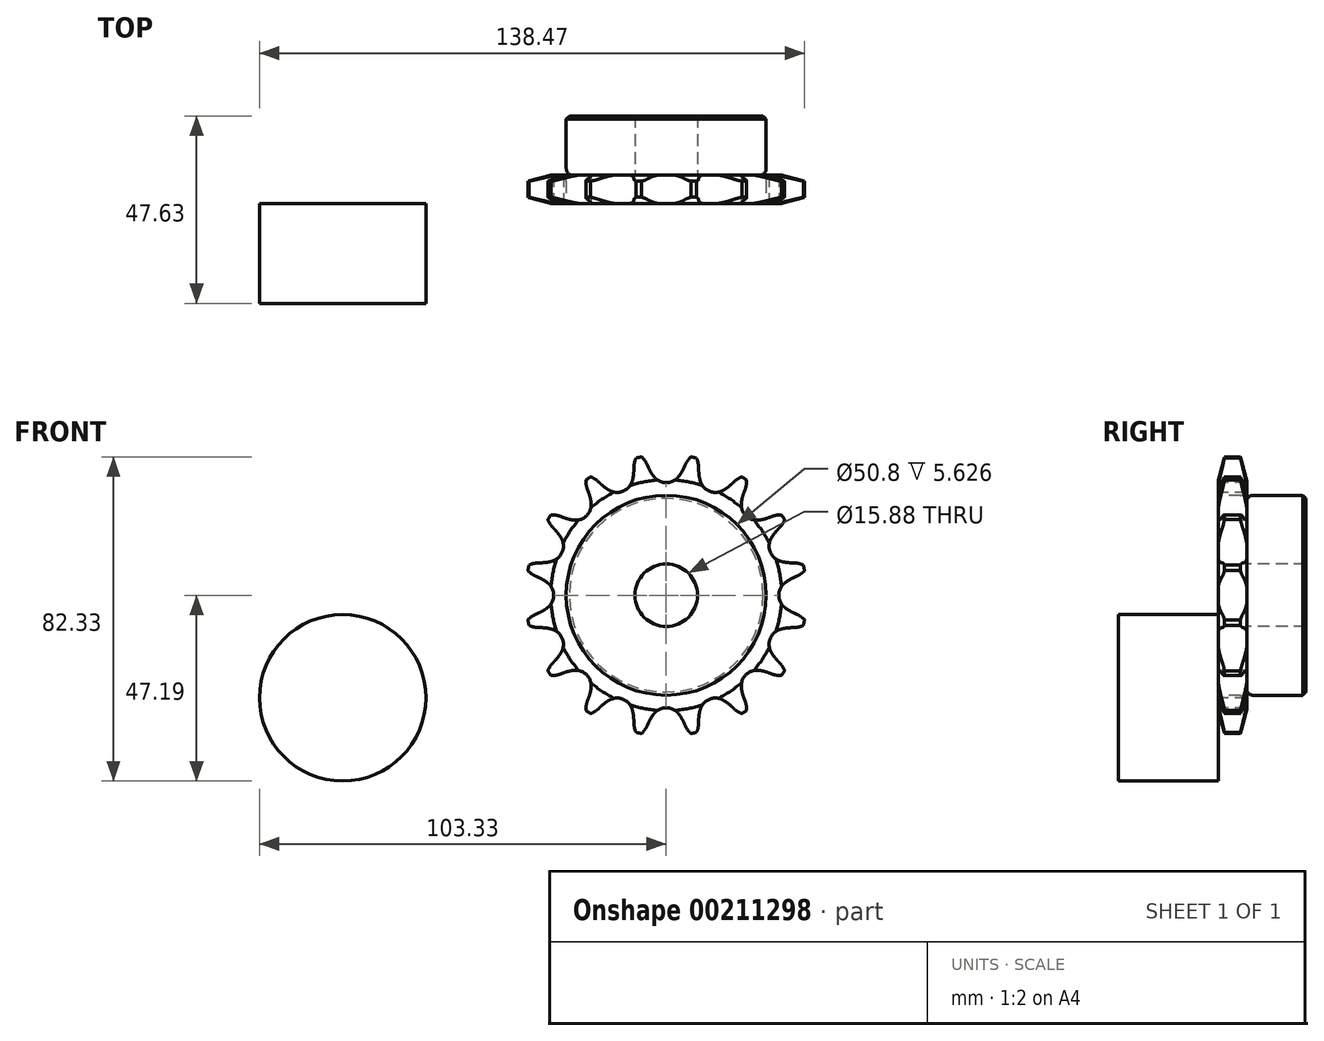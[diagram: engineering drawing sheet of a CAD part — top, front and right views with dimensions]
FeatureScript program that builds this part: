
annotation { "Feature Type Name" : "Feature", "Feature Type Description" : "" }
export const myFeature = defineFeature(function(context is Context, id is Id, definition is map)
    precondition{}
    {
        {
            var Q0;
            Q0=qCreatedBy(makeId("Right.planeOp"),FACE);
            var sketch = newSketch(context, id + "F0", { "sketchPlane" : qUnion([Q0])});
            skLineSegment(sketch, "E0", {"start": v(0, 0) * mm, "end": v(22.23, 0) * mm, "construction": true});
            skLineSegment(sketch, "E1.bottom", {"start": v(0, 7.94) * mm, "end": v(7.21, 7.94) * mm});
            skLineSegment(sketch, "E1.top", {"start": v(0, 35.69) * mm, "end": v(7.21, 35.69) * mm});
            skLineSegment(sketch, "E1.left", {"start": v(0, 7.94) * mm, "end": v(0, 35.69) * mm});
            skLineSegment(sketch, "E1.right", {"start": v(7.21, 7.94) * mm, "end": v(7.21, 35.69) * mm});
            skLineSegment(sketch, "E2.bottom", {"start": v(0, 7.94) * mm, "end": v(22.23, 7.94) * mm});
            skLineSegment(sketch, "E2.top", {"start": v(0, 25.4) * mm, "end": v(22.23, 25.4) * mm});
            skLineSegment(sketch, "E2.left", {"start": v(0, 7.94) * mm, "end": v(0, 25.4) * mm});
            skLineSegment(sketch, "E2.right", {"start": v(22.23, 7.94) * mm, "end": v(22.23, 25.4) * mm});
            skLineSegment(sketch, "E3.MirrorCS", {"start": v(0, -7.94) * mm, "end": v(7.21, -7.94) * mm});
            skLineSegment(sketch, "E4.MirrorCS", {"start": v(0, -25.4) * mm, "end": v(22.23, -25.4) * mm});
            skLineSegment(sketch, "E5.MirrorCS", {"start": v(0, -7.94) * mm, "end": v(22.23, -7.94) * mm});
            skLineSegment(sketch, "E6.MirrorCS", {"start": v(7.21, -7.94) * mm, "end": v(7.21, -35.69) * mm});
            skLineSegment(sketch, "E7.MirrorCS", {"start": v(0, -7.94) * mm, "end": v(0, -35.69) * mm});
            skLineSegment(sketch, "E8.MirrorCS", {"start": v(22.23, -7.94) * mm, "end": v(22.23, -25.4) * mm});
            skLineSegment(sketch, "E9.MirrorCS", {"start": v(0, -7.94) * mm, "end": v(0, -25.4) * mm});
            skLineSegment(sketch, "E10.MirrorCS", {"start": v(0, -35.69) * mm, "end": v(7.21, -35.69) * mm});
            skSolve(sketch);
        }
        {
            var Q0;
            {var subQ0=sQuery(id+"F0.wireOp",EDGE,"E1.top");Q0=makeQuery(id+"F0.imprint","IMPRINT",FACE,{"disambiguationData":[TD([[makeQuery(id+"F0.imprint","IMPRINT",EDGE,{"derivedFrom":subQ0}),-1.0]])]});}
            var Q1;
            {var subQ5=sQuery(id+"F0.wireOp",EDGE,"E2.left");Q1=makeQuery(id+"F0.imprint","IMPRINT",FACE,{"disambiguationData":[TD([[makeQuery(id+"F0.imprint","IMPRINT",EDGE,{"derivedFrom":subQ5}),-1.0]])]});}
            var Q2;
            {var subQ5=sQuery(id+"F0.wireOp",EDGE,"E2.right");Q2=makeQuery(id+"F0.imprint","IMPRINT",FACE,{"disambiguationData":[TD([[makeQuery(id+"F0.imprint","IMPRINT",EDGE,{"derivedFrom":subQ5}),1.0]])]});}
            var Q3;
            Q3=sQuery(id+"F0.wireOp",EDGE,"E0");
            revolve(context, id + "F1", {"entities" : qUnion([Q0, Q1, Q2]), "axis" : qUnion([Q3]), "revolveType" : RevolveType.FULL});
        }
        {
            var Q0;
            Q0=makeQuery(id+"F1.opRevolve","SWEPT_EDGE",EDGE,{"disambiguationData":[OSD([sQuery(id+"F0.wireOp",EDGE,"E1.right"),sQuery(id+"F0.wireOp",EDGE,"E2.top")])]});
            fillet(context, id + "F2", {"entities" : qUnion([Q0]), "radius" : 1.59 * mm, "tangentPropagation" : true, "allowEdgeOverflow" : false});
        }
        {
            var Q0;
            Q0=makeQuery(id+"F1.opRevolve","SWEPT_EDGE",EDGE,{"disambiguationData":[OSD([sQuery(id+"F0.wireOp",EDGE,"E2.top"),sQuery(id+"F0.wireOp",EDGE,"E2.right")])]});
            chamfer(context, id + "F3", {"entities" : qUnion([Q0]), "width" : 0.8 * mm, "tangentPropagation" : true});
        }
        {
            var Q0;
            Q0=makeQuery(id+"F1.opRevolve","SWEPT_EDGE",EDGE,{"disambiguationData":[OSD([sQuery(id+"F0.wireOp",EDGE,"E1.top"),sQuery(id+"F0.wireOp",EDGE,"E1.left")])]});
            var Q1;
            Q1=makeQuery(id+"F1.opRevolve","SWEPT_EDGE",EDGE,{"disambiguationData":[OSD([sQuery(id+"F0.wireOp",EDGE,"E1.top"),sQuery(id+"F0.wireOp",EDGE,"E1.right")])]});
            chamfer(context, id + "F4", {"entities" : qUnion([Q0, Q1]), "chamferType" : ChamferType.TWO_OFFSETS, "width1" : 6.35 * mm, "oppositeDirection" : false, "width2" : 1.57 * mm, "tangentPropagation" : true});
        }
        {
            var Q0;
            Q0=makeQuery(id+"F1.opRevolve","SWEPT_FACE",FACE,{"disambiguationData":[OSD([sQuery(id+"F0.wireOp",EDGE,"E1.left"),sQuery(id+"F0.wireOp",EDGE,"E2.left")])]});
            var sketch = newSketch(context, id + "F5", { "sketchPlane" : qUnion([Q0])});
            skArc(sketch, "E11", {"start": v(-4.8, 33.1) * mm, "mid": v(-5.78, 34.65) * mm, "end": v(-7.13, 35.87) * mm});
            skLineSegment(sketch, "E12", {"start": v(-4.45, 32.3) * mm, "end": v(-4.8, 33.1) * mm});
            skArc(sketch, "E13", {"start": v(-4.45, 32.3) * mm, "mid": v(-3.84, 31.15) * mm, "end": v(-3.1, 30.08) * mm});
            skArc(sketch, "E14", {"start": v(-3.1, 30.08) * mm, "mid": v(0.01, 28.6) * mm, "end": v(3.1, 30.1) * mm});
            skArc(sketch, "E15.MirrorCS", {"start": v(4.46, 32.32) * mm, "mid": v(3.85, 31.17) * mm, "end": v(3.1, 30.1) * mm});
            skLineSegment(sketch, "E16.MirrorCS", {"start": v(4.46, 32.32) * mm, "end": v(4.82, 33.12) * mm});
            skArc(sketch, "E17.MirrorCS", {"start": v(4.82, 33.12) * mm, "mid": v(5.79, 34.66) * mm, "end": v(7.14, 35.87) * mm});
            skLineSegment(sketch, "E18", {"start": v(0, 0) * mm, "end": v(0, 32.56) * mm, "construction": true});
            skArc(sketch, "E19.1.0", {"start": v(-17.1, 28.74) * mm, "mid": v(-18.6, 29.8) * mm, "end": v(-20.32, 30.41) * mm});
            skLineSegment(sketch, "E19.1.1", {"start": v(-16.47, 28.14) * mm, "end": v(-17.1, 28.74) * mm});
            skArc(sketch, "E19.1.2", {"start": v(-16.47, 28.14) * mm, "mid": v(-15.47, 27.3) * mm, "end": v(-14.37, 26.61) * mm});
            skArc(sketch, "E19.1.3", {"start": v(-14.37, 26.61) * mm, "mid": v(-10.93, 26.43) * mm, "end": v(-8.65, 29) * mm});
            skArc(sketch, "E19.1.4", {"start": v(-8.25, 31.57) * mm, "mid": v(-8.37, 30.27) * mm, "end": v(-8.65, 29) * mm});
            skLineSegment(sketch, "E19.1.5", {"start": v(-8.25, 31.57) * mm, "end": v(-8.22, 32.44) * mm});
            skArc(sketch, "E19.1.6", {"start": v(-8.22, 32.44) * mm, "mid": v(-7.91, 34.23) * mm, "end": v(-7.13, 35.87) * mm});
            skArc(sketch, "E19.2.0", {"start": v(-26.8, 20) * mm, "mid": v(-28.59, 20.42) * mm, "end": v(-30.4, 20.32) * mm});
            skLineSegment(sketch, "E19.2.1", {"start": v(-25.99, 19.7) * mm, "end": v(-26.8, 20) * mm});
            skArc(sketch, "E19.2.2", {"start": v(-25.99, 19.7) * mm, "mid": v(-24.74, 19.31) * mm, "end": v(-23.46, 19.09) * mm});
            skArc(sketch, "E19.2.3", {"start": v(-23.46, 19.09) * mm, "mid": v(-20.22, 20.23) * mm, "end": v(-19.09, 23.48) * mm});
            skArc(sketch, "E19.2.4", {"start": v(-19.7, 26.01) * mm, "mid": v(-19.31, 24.76) * mm, "end": v(-19.09, 23.48) * mm});
            skLineSegment(sketch, "E19.2.5", {"start": v(-19.7, 26.01) * mm, "end": v(-20, 26.83) * mm});
            skArc(sketch, "E19.2.6", {"start": v(-20, 26.83) * mm, "mid": v(-20.41, 28.6) * mm, "end": v(-20.32, 30.41) * mm});
            skArc(sketch, "E19.3.0", {"start": v(-32.42, 8.22) * mm, "mid": v(-34.22, 7.92) * mm, "end": v(-35.87, 7.14) * mm});
            skLineSegment(sketch, "E19.3.1", {"start": v(-31.55, 8.25) * mm, "end": v(-32.42, 8.22) * mm});
            skArc(sketch, "E19.3.2", {"start": v(-31.55, 8.25) * mm, "mid": v(-30.25, 8.37) * mm, "end": v(-28.98, 8.66) * mm});
            skArc(sketch, "E19.3.3", {"start": v(-28.98, 8.66) * mm, "mid": v(-26.42, 10.96) * mm, "end": v(-26.62, 14.39) * mm});
            skArc(sketch, "E19.3.4", {"start": v(-28.15, 16.5) * mm, "mid": v(-27.32, 15.49) * mm, "end": v(-26.62, 14.39) * mm});
            skLineSegment(sketch, "E19.3.5", {"start": v(-28.15, 16.5) * mm, "end": v(-28.75, 17.13) * mm});
            skArc(sketch, "E19.3.6", {"start": v(-28.75, 17.13) * mm, "mid": v(-29.8, 18.61) * mm, "end": v(-30.4, 20.32) * mm});
            skArc(sketch, "E19.4.0", {"start": v(-33.1, -4.8) * mm, "mid": v(-34.65, -5.78) * mm, "end": v(-35.87, -7.13) * mm});
            skLineSegment(sketch, "E19.4.1", {"start": v(-32.3, -4.45) * mm, "end": v(-33.1, -4.8) * mm});
            skArc(sketch, "E19.4.2", {"start": v(-32.3, -4.45) * mm, "mid": v(-31.15, -3.84) * mm, "end": v(-30.08, -3.1) * mm});
            skArc(sketch, "E19.4.3", {"start": v(-30.08, -3.1) * mm, "mid": v(-28.6, 0.01) * mm, "end": v(-30.1, 3.1) * mm});
            skArc(sketch, "E19.4.4", {"start": v(-32.32, 4.46) * mm, "mid": v(-31.17, 3.85) * mm, "end": v(-30.1, 3.1) * mm});
            skLineSegment(sketch, "E19.4.5", {"start": v(-32.32, 4.46) * mm, "end": v(-33.12, 4.82) * mm});
            skArc(sketch, "E19.4.6", {"start": v(-33.12, 4.82) * mm, "mid": v(-34.66, 5.79) * mm, "end": v(-35.87, 7.14) * mm});
            skArc(sketch, "E19.5.0", {"start": v(-28.74, -17.1) * mm, "mid": v(-29.8, -18.6) * mm, "end": v(-30.41, -20.32) * mm});
            skLineSegment(sketch, "E19.5.1", {"start": v(-28.14, -16.47) * mm, "end": v(-28.74, -17.1) * mm});
            skArc(sketch, "E19.5.2", {"start": v(-28.14, -16.47) * mm, "mid": v(-27.3, -15.47) * mm, "end": v(-26.61, -14.37) * mm});
            skArc(sketch, "E19.5.3", {"start": v(-26.61, -14.37) * mm, "mid": v(-26.43, -10.93) * mm, "end": v(-29, -8.65) * mm});
            skArc(sketch, "E19.5.4", {"start": v(-31.57, -8.25) * mm, "mid": v(-30.27, -8.37) * mm, "end": v(-29, -8.65) * mm});
            skLineSegment(sketch, "E19.5.5", {"start": v(-31.57, -8.25) * mm, "end": v(-32.44, -8.22) * mm});
            skArc(sketch, "E19.5.6", {"start": v(-32.44, -8.22) * mm, "mid": v(-34.23, -7.91) * mm, "end": v(-35.87, -7.13) * mm});
            skArc(sketch, "E19.6.0", {"start": v(-20, -26.8) * mm, "mid": v(-20.42, -28.59) * mm, "end": v(-20.32, -30.4) * mm});
            skLineSegment(sketch, "E19.6.1", {"start": v(-19.7, -25.99) * mm, "end": v(-20, -26.8) * mm});
            skArc(sketch, "E19.6.2", {"start": v(-19.7, -25.99) * mm, "mid": v(-19.31, -24.74) * mm, "end": v(-19.09, -23.46) * mm});
            skArc(sketch, "E19.6.3", {"start": v(-19.09, -23.46) * mm, "mid": v(-20.23, -20.22) * mm, "end": v(-23.48, -19.09) * mm});
            skArc(sketch, "E19.6.4", {"start": v(-26.01, -19.7) * mm, "mid": v(-24.76, -19.31) * mm, "end": v(-23.48, -19.09) * mm});
            skLineSegment(sketch, "E19.6.5", {"start": v(-26.01, -19.7) * mm, "end": v(-26.83, -20) * mm});
            skArc(sketch, "E19.6.6", {"start": v(-26.83, -20) * mm, "mid": v(-28.6, -20.41) * mm, "end": v(-30.41, -20.32) * mm});
            skArc(sketch, "E19.7.0", {"start": v(-8.22, -32.42) * mm, "mid": v(-7.92, -34.22) * mm, "end": v(-7.14, -35.87) * mm});
            skLineSegment(sketch, "E19.7.1", {"start": v(-8.25, -31.55) * mm, "end": v(-8.22, -32.42) * mm});
            skArc(sketch, "E19.7.2", {"start": v(-8.25, -31.55) * mm, "mid": v(-8.37, -30.25) * mm, "end": v(-8.66, -28.98) * mm});
            skArc(sketch, "E19.7.3", {"start": v(-8.66, -28.98) * mm, "mid": v(-10.96, -26.42) * mm, "end": v(-14.39, -26.62) * mm});
            skArc(sketch, "E19.7.4", {"start": v(-16.5, -28.15) * mm, "mid": v(-15.49, -27.32) * mm, "end": v(-14.39, -26.62) * mm});
            skLineSegment(sketch, "E19.7.5", {"start": v(-16.5, -28.15) * mm, "end": v(-17.13, -28.75) * mm});
            skArc(sketch, "E19.7.6", {"start": v(-17.13, -28.75) * mm, "mid": v(-18.61, -29.8) * mm, "end": v(-20.32, -30.4) * mm});
            skArc(sketch, "E19.8.0", {"start": v(4.8, -33.1) * mm, "mid": v(5.78, -34.65) * mm, "end": v(7.13, -35.87) * mm});
            skLineSegment(sketch, "E19.8.1", {"start": v(4.45, -32.3) * mm, "end": v(4.8, -33.1) * mm});
            skArc(sketch, "E19.8.2", {"start": v(4.45, -32.3) * mm, "mid": v(3.84, -31.15) * mm, "end": v(3.1, -30.08) * mm});
            skArc(sketch, "E19.8.3", {"start": v(3.1, -30.08) * mm, "mid": v(-0.01, -28.6) * mm, "end": v(-3.1, -30.1) * mm});
            skArc(sketch, "E19.8.4", {"start": v(-4.46, -32.32) * mm, "mid": v(-3.85, -31.17) * mm, "end": v(-3.1, -30.1) * mm});
            skLineSegment(sketch, "E19.8.5", {"start": v(-4.46, -32.32) * mm, "end": v(-4.82, -33.12) * mm});
            skArc(sketch, "E19.8.6", {"start": v(-4.82, -33.12) * mm, "mid": v(-5.79, -34.66) * mm, "end": v(-7.14, -35.87) * mm});
            skArc(sketch, "E19.9.0", {"start": v(17.1, -28.74) * mm, "mid": v(18.6, -29.8) * mm, "end": v(20.32, -30.41) * mm});
            skLineSegment(sketch, "E19.9.1", {"start": v(16.47, -28.14) * mm, "end": v(17.1, -28.74) * mm});
            skArc(sketch, "E19.9.2", {"start": v(16.47, -28.14) * mm, "mid": v(15.47, -27.3) * mm, "end": v(14.37, -26.61) * mm});
            skArc(sketch, "E19.9.3", {"start": v(14.37, -26.61) * mm, "mid": v(10.93, -26.43) * mm, "end": v(8.65, -29) * mm});
            skArc(sketch, "E19.9.4", {"start": v(8.25, -31.57) * mm, "mid": v(8.37, -30.27) * mm, "end": v(8.65, -29) * mm});
            skLineSegment(sketch, "E19.9.5", {"start": v(8.25, -31.57) * mm, "end": v(8.22, -32.44) * mm});
            skArc(sketch, "E19.9.6", {"start": v(8.22, -32.44) * mm, "mid": v(7.91, -34.23) * mm, "end": v(7.13, -35.87) * mm});
            skArc(sketch, "E19.10.0", {"start": v(26.8, -20) * mm, "mid": v(28.59, -20.42) * mm, "end": v(30.4, -20.32) * mm});
            skLineSegment(sketch, "E19.10.1", {"start": v(25.99, -19.7) * mm, "end": v(26.8, -20) * mm});
            skArc(sketch, "E19.10.2", {"start": v(25.99, -19.7) * mm, "mid": v(24.74, -19.31) * mm, "end": v(23.46, -19.09) * mm});
            skArc(sketch, "E19.10.3", {"start": v(23.46, -19.09) * mm, "mid": v(20.22, -20.23) * mm, "end": v(19.09, -23.48) * mm});
            skArc(sketch, "E19.10.4", {"start": v(19.7, -26.01) * mm, "mid": v(19.31, -24.76) * mm, "end": v(19.09, -23.48) * mm});
            skLineSegment(sketch, "E19.10.5", {"start": v(19.7, -26.01) * mm, "end": v(20, -26.83) * mm});
            skArc(sketch, "E19.10.6", {"start": v(20, -26.83) * mm, "mid": v(20.41, -28.6) * mm, "end": v(20.32, -30.41) * mm});
            skArc(sketch, "E19.11.0", {"start": v(32.42, -8.22) * mm, "mid": v(34.22, -7.92) * mm, "end": v(35.87, -7.14) * mm});
            skLineSegment(sketch, "E19.11.1", {"start": v(31.55, -8.25) * mm, "end": v(32.42, -8.22) * mm});
            skArc(sketch, "E19.11.2", {"start": v(31.55, -8.25) * mm, "mid": v(30.25, -8.37) * mm, "end": v(28.98, -8.66) * mm});
            skArc(sketch, "E19.11.3", {"start": v(28.98, -8.66) * mm, "mid": v(26.42, -10.96) * mm, "end": v(26.62, -14.39) * mm});
            skArc(sketch, "E19.11.4", {"start": v(28.15, -16.5) * mm, "mid": v(27.32, -15.49) * mm, "end": v(26.62, -14.39) * mm});
            skLineSegment(sketch, "E19.11.5", {"start": v(28.15, -16.5) * mm, "end": v(28.75, -17.13) * mm});
            skArc(sketch, "E19.11.6", {"start": v(28.75, -17.13) * mm, "mid": v(29.8, -18.61) * mm, "end": v(30.4, -20.32) * mm});
            skArc(sketch, "E19.12.0", {"start": v(33.1, 4.8) * mm, "mid": v(34.65, 5.78) * mm, "end": v(35.87, 7.13) * mm});
            skLineSegment(sketch, "E19.12.1", {"start": v(32.3, 4.45) * mm, "end": v(33.1, 4.8) * mm});
            skArc(sketch, "E19.12.2", {"start": v(32.3, 4.45) * mm, "mid": v(31.15, 3.84) * mm, "end": v(30.08, 3.1) * mm});
            skArc(sketch, "E19.12.3", {"start": v(30.08, 3.1) * mm, "mid": v(28.6, -0.01) * mm, "end": v(30.1, -3.1) * mm});
            skArc(sketch, "E19.12.4", {"start": v(32.32, -4.46) * mm, "mid": v(31.17, -3.85) * mm, "end": v(30.1, -3.1) * mm});
            skLineSegment(sketch, "E19.12.5", {"start": v(32.32, -4.46) * mm, "end": v(33.12, -4.82) * mm});
            skArc(sketch, "E19.12.6", {"start": v(33.12, -4.82) * mm, "mid": v(34.66, -5.79) * mm, "end": v(35.87, -7.14) * mm});
            skArc(sketch, "E19.13.0", {"start": v(28.74, 17.1) * mm, "mid": v(29.8, 18.6) * mm, "end": v(30.41, 20.32) * mm});
            skLineSegment(sketch, "E19.13.1", {"start": v(28.14, 16.47) * mm, "end": v(28.74, 17.1) * mm});
            skArc(sketch, "E19.13.2", {"start": v(28.14, 16.47) * mm, "mid": v(27.3, 15.47) * mm, "end": v(26.61, 14.37) * mm});
            skArc(sketch, "E19.13.3", {"start": v(26.61, 14.37) * mm, "mid": v(26.43, 10.93) * mm, "end": v(29, 8.65) * mm});
            skArc(sketch, "E19.13.4", {"start": v(31.57, 8.25) * mm, "mid": v(30.27, 8.37) * mm, "end": v(29, 8.65) * mm});
            skLineSegment(sketch, "E19.13.5", {"start": v(31.57, 8.25) * mm, "end": v(32.44, 8.22) * mm});
            skArc(sketch, "E19.13.6", {"start": v(32.44, 8.22) * mm, "mid": v(34.23, 7.91) * mm, "end": v(35.87, 7.13) * mm});
            skArc(sketch, "E19.14.0", {"start": v(20, 26.8) * mm, "mid": v(20.42, 28.59) * mm, "end": v(20.32, 30.4) * mm});
            skLineSegment(sketch, "E19.14.1", {"start": v(19.7, 25.99) * mm, "end": v(20, 26.8) * mm});
            skArc(sketch, "E19.14.2", {"start": v(19.7, 25.99) * mm, "mid": v(19.31, 24.74) * mm, "end": v(19.09, 23.46) * mm});
            skArc(sketch, "E19.14.3", {"start": v(19.09, 23.46) * mm, "mid": v(20.23, 20.22) * mm, "end": v(23.48, 19.09) * mm});
            skArc(sketch, "E19.14.4", {"start": v(26.01, 19.7) * mm, "mid": v(24.76, 19.31) * mm, "end": v(23.48, 19.09) * mm});
            skLineSegment(sketch, "E19.14.5", {"start": v(26.01, 19.7) * mm, "end": v(26.83, 20) * mm});
            skArc(sketch, "E19.14.6", {"start": v(26.83, 20) * mm, "mid": v(28.6, 20.41) * mm, "end": v(30.41, 20.32) * mm});
            skArc(sketch, "E19.15.0", {"start": v(8.22, 32.42) * mm, "mid": v(7.92, 34.22) * mm, "end": v(7.14, 35.87) * mm});
            skLineSegment(sketch, "E19.15.1", {"start": v(8.25, 31.55) * mm, "end": v(8.22, 32.42) * mm});
            skArc(sketch, "E19.15.2", {"start": v(8.25, 31.55) * mm, "mid": v(8.37, 30.25) * mm, "end": v(8.66, 28.98) * mm});
            skArc(sketch, "E19.15.3", {"start": v(8.66, 28.98) * mm, "mid": v(10.96, 26.42) * mm, "end": v(14.39, 26.62) * mm});
            skArc(sketch, "E19.15.4", {"start": v(16.5, 28.15) * mm, "mid": v(15.49, 27.32) * mm, "end": v(14.39, 26.62) * mm});
            skLineSegment(sketch, "E19.15.5", {"start": v(16.5, 28.15) * mm, "end": v(17.13, 28.75) * mm});
            skArc(sketch, "E19.15.6", {"start": v(17.13, 28.75) * mm, "mid": v(18.61, 29.8) * mm, "end": v(20.32, 30.4) * mm});
            skPoint(sketch, "E19.center", {"position": v(0, 0) * mm});
            skSolve(sketch);
        }
        {
            var Q0;
            Q0=qSketchRegion(id+"F5",true);
            extrude(context, id + "F6", {"entities" : qUnion([Q0]), "operationType" : NewBodyOperationType.INTERSECT, "endBound" : BoundingType.THROUGH_ALL, "oppositeDirection" : true, "depth" : 25.4 * mm});
        }
        {
            var Q0;
            Q0=qCreatedBy(makeId("Front.planeOp"),FACE);
            var sketch = newSketch(context, id + "F7", { "sketchPlane" : qUnion([Q0])});
            skCircle(sketch, "E20", {"center": v(-82.2, -26.06) * mm, "radius": 21.13 * mm});
            skSolve(sketch);
        }
        {
            var Q0;
            Q0=makeQuery(id+"F7.imprint","IMPRINT",FACE,{"disambiguationData":[TD([[makeQuery(id+"F7.imprint","IMPRINT",EDGE,{"derivedFrom":sQuery(id+"F7.wireOp",EDGE,"E20")}),1.0]])]});
            extrude(context, id + "F8", {"entities" : qUnion([Q0]), "depth" : 25.4 * mm});
        }
    });
